# Revit family: ELC 83000
name_source: partatom
category: Plumbing Fixtures
revit_build: Autodesk Revit 2018 (Build: 20170223_1515(x64)
units: mm (PartAtom-declared; Revit-internal decimal feet)

## family parameters
Cut with Voids When Loaded = No
Host = Face
OmniClass Number = 23.45.05.14.14
OmniClass Title = Sinks/Lavatories
Part Type = Normal
Room Calculation Point = No
Round Connector Dimension = Use Diameter
Shared = No

## types (1)
- ELC 83000
    ADA Compliant = Yes
    CW Connection = Yes
    CWFU = 0
    Cold Water Connection Diameter = 3/4"
    Default Elevation = 27"
    Description = SloanStone® 3-Station Wall-Mounted Counter Top Sink
    HW Connection = Yes
    HWFU = 0
    Hot Water Connection Diameter = 3/4"
    Manufacturer = SLOAN
    Model = ELC-83000
    Price = Prices may vary. Please consult Manufacturer Representative for most up-to-date price list
    Product Documentation Link = https://www.sloan.com
    Product Page URL = https://www.sloan.com
    Sink Material = <By Category>
    URL = https://www.sloan.com
    Vent Connection = No
    Voltage = 120 V
    WFU = 0
    Waste Connection = Yes
    Waste Water Connection Diameter = 1 3/4"

## geometry (parser evidence)
native form markers: Sweep x2
no freeform markers — native parametric forms only
